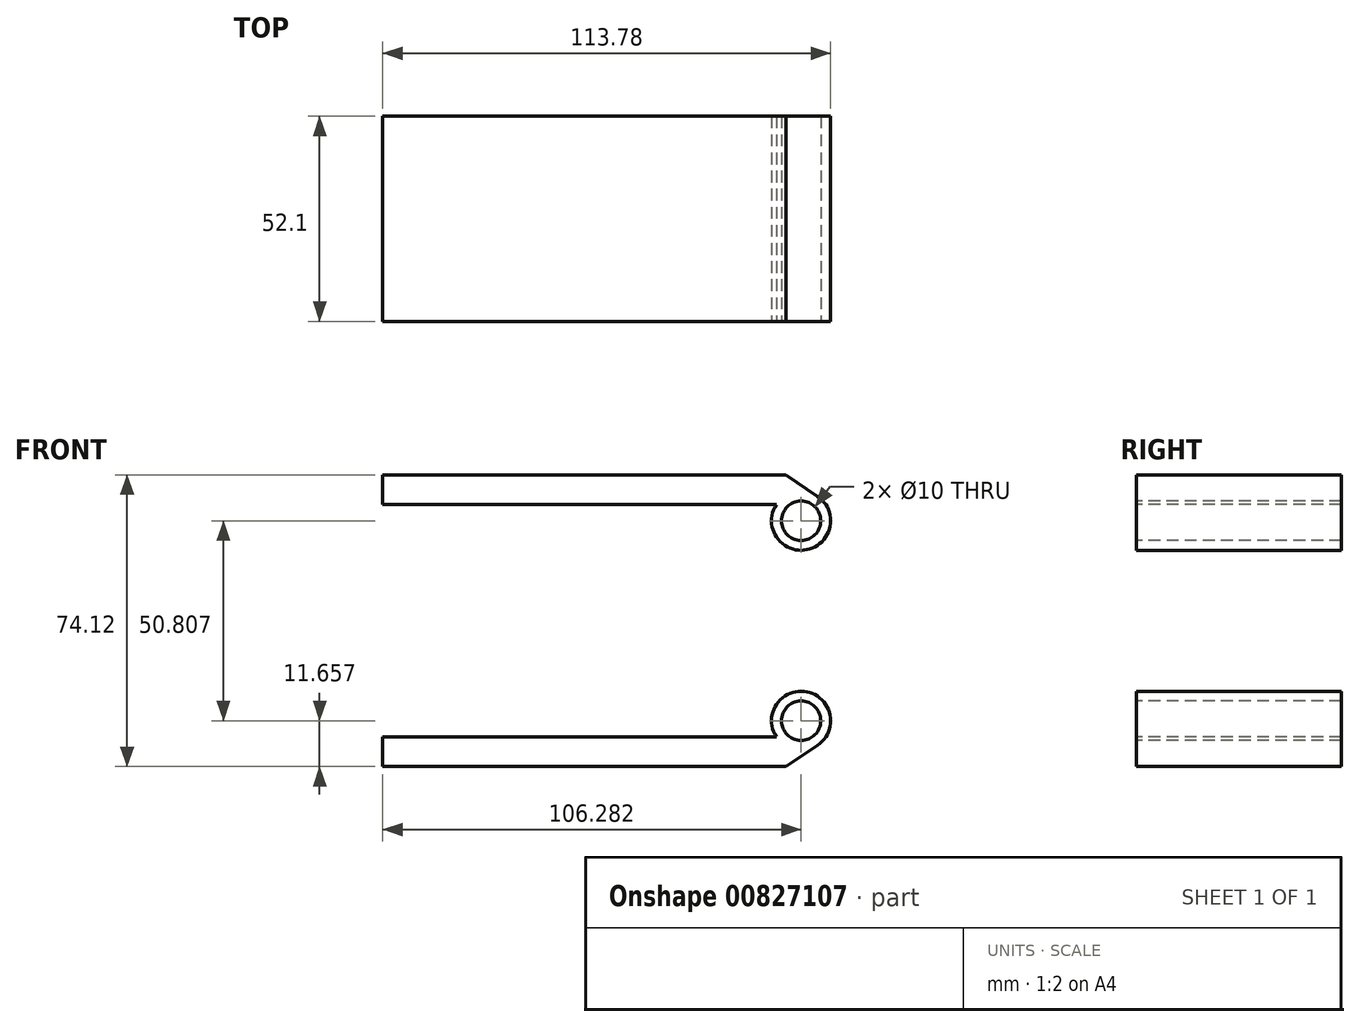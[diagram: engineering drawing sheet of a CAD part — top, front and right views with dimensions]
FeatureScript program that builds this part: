
annotation { "Feature Type Name" : "Feature", "Feature Type Description" : "" }
export const myFeature = defineFeature(function(context is Context, id is Id, definition is map)
    precondition{}
    {
        {
            var Q0;
            Q0=qCreatedBy(makeId("Front.planeOp"),FACE);
            var sketch = newSketch(context, id + "F0", { "sketchPlane" : qUnion([Q0])});
            skLineSegment(sketch, "E0.bottom", {"start": v(-62.3, 0) * mm, "end": v(37.7, 0) * mm});
            skLineSegment(sketch, "E0.top", {"start": v(-62.3, -7.56) * mm, "end": v(40.12, -7.56) * mm});
            skLineSegment(sketch, "E0.left", {"start": v(-62.3, 0) * mm, "end": v(-62.3, -7.56) * mm});
            skArc(sketch, "E1", {"start": v(48.17, -2.12) * mm, "mid": v(45.46, 11.45) * mm, "end": v(37.7, 0) * mm});
            skCircle(sketch, "E2", {"center": v(43.97, 4.1) * mm, "radius": 5 * mm});
            skLineSegment(sketch, "E3", {"start": v(37.7, 0) * mm, "end": v(37.7, 0) * mm});
            skLineSegment(sketch, "E4", {"start": v(40.12, -7.56) * mm, "end": v(48.17, -2.12) * mm});
            skSolve(sketch);
        }
        {
            var Q0;
            Q0=makeQuery(id+"F0.imprint","IMPRINT",FACE,{"disambiguationData":[TD([[makeQuery(id+"F0.imprint","IMPRINT",EDGE,{"derivedFrom":sQuery(id+"F0.wireOp",EDGE,"E0.bottom")}),-1.0]])]});
            extrude(context, id + "F1", {"entities" : qUnion([Q0]), "oppositeDirection" : true, "depth" : 52.1 * mm, "offsetDistance" : 25 * mm});
        }
        {
            var Q0;
            Q0=qCreatedBy(makeId("Top.planeOp"),FACE);
            cPlane(context, id + "F2", {"entities" : qUnion([Q0]), "cplaneType" : CPlaneType.OFFSET, "offset" : 29.5 * mm, "width" : 150 * mm, "height" : 150 * mm});
        }
        {
            var Q0;
            Q0=makeQuery(id+"F1.opExtrude","SWEPT_BODY",BODY,{"disambiguationData":[OSD([sQuery(id+"F0.wireOp",EDGE,"E0.bottom"),sQuery(id+"F0.wireOp",EDGE,"E0.top"),sQuery(id+"F0.wireOp",EDGE,"E0.left"),sQuery(id+"F0.wireOp",EDGE,"E1"),sQuery(id+"F0.wireOp",EDGE,"E2"),sQuery(id+"F0.wireOp",EDGE,"E3"),sQuery(id+"F0.wireOp",EDGE,"E4")])]});
            var Q1;
            Q1=qCreatedBy(id+"F2.planeOp",FACE);
            mirror(context, id + "F3", {"entities" : qUnion([Q0]), "mirrorPlane" : qUnion([Q1])});
        }
    });
